FCSTD DOCUMENT  (FreeCAD 0.22R37730 (Git))
Label: вешалка
License: All rights reserved
LicenseURL: https://en.wikipedia.org/wiki/All_rights_reserved
objects: Sketcher::SketchObject×1, PartDesign::Body×1, App::Part×1
note: 2 computed .brp shape members not serialized (recipe doc carries the construction recipe); baked Part::Feature solids carry a one-line shape summary decoded from their .brp

FEATURE [Sketcher::SketchObject] Sketch
  AttachmentSupport = -> [XZ_Plane001]
  FullyConstrained = false
  MapMode = 5
  Placement = pos=(0,0,0) rot=(1,0,0;1.5708rad)
  Support = -> [XZ_Plane001]
  sketch-geometry (6):
    g0: LineSegment StartX=0 StartY=0 StartZ=0 EndX=0 EndY=30.0622 EndZ=0
    g1: LineSegment StartX=0 StartY=0 StartZ=0 EndX=4.52434 EndY=0 EndZ=0
    g2: LineSegment StartX=4.52434 StartY=0 StartZ=0 EndX=4.52434 EndY=28.8352 EndZ=0
    g3: LineSegment StartX=4.52434 StartY=28.8352 StartZ=0 EndX=16.4875 EndY=42.6389 EndZ=0
    g4: LineSegment StartX=16.4875 StartY=42.6389 StartZ=0 EndX=14.4937 EndY=42.4855 EndZ=0
    g5: LineSegment StartX=14.4937 StartY=42.4855 StartZ=0 EndX=0 EndY=30.0622 EndZ=0
  constraints (8):
    c: Coincident(g0,g-1)
    c: PointOnObject(g0,g-2)
    c: Coincident(g1,g0)
    c: PointOnObject(g1,g-1)
    c: Coincident(g2,g1)
    c: Vertical(g2)
    c: Coincident(g3,g2)
    c: Coincident(g5,g0)
FEATURE [PartDesign::Body] Body
  AllowCompound = false
  Group = -> [Sketch]
  Origin = -> Origin001
FEATURE [App::Part] Part
  Group = -> [Body]
  Origin = -> Origin
